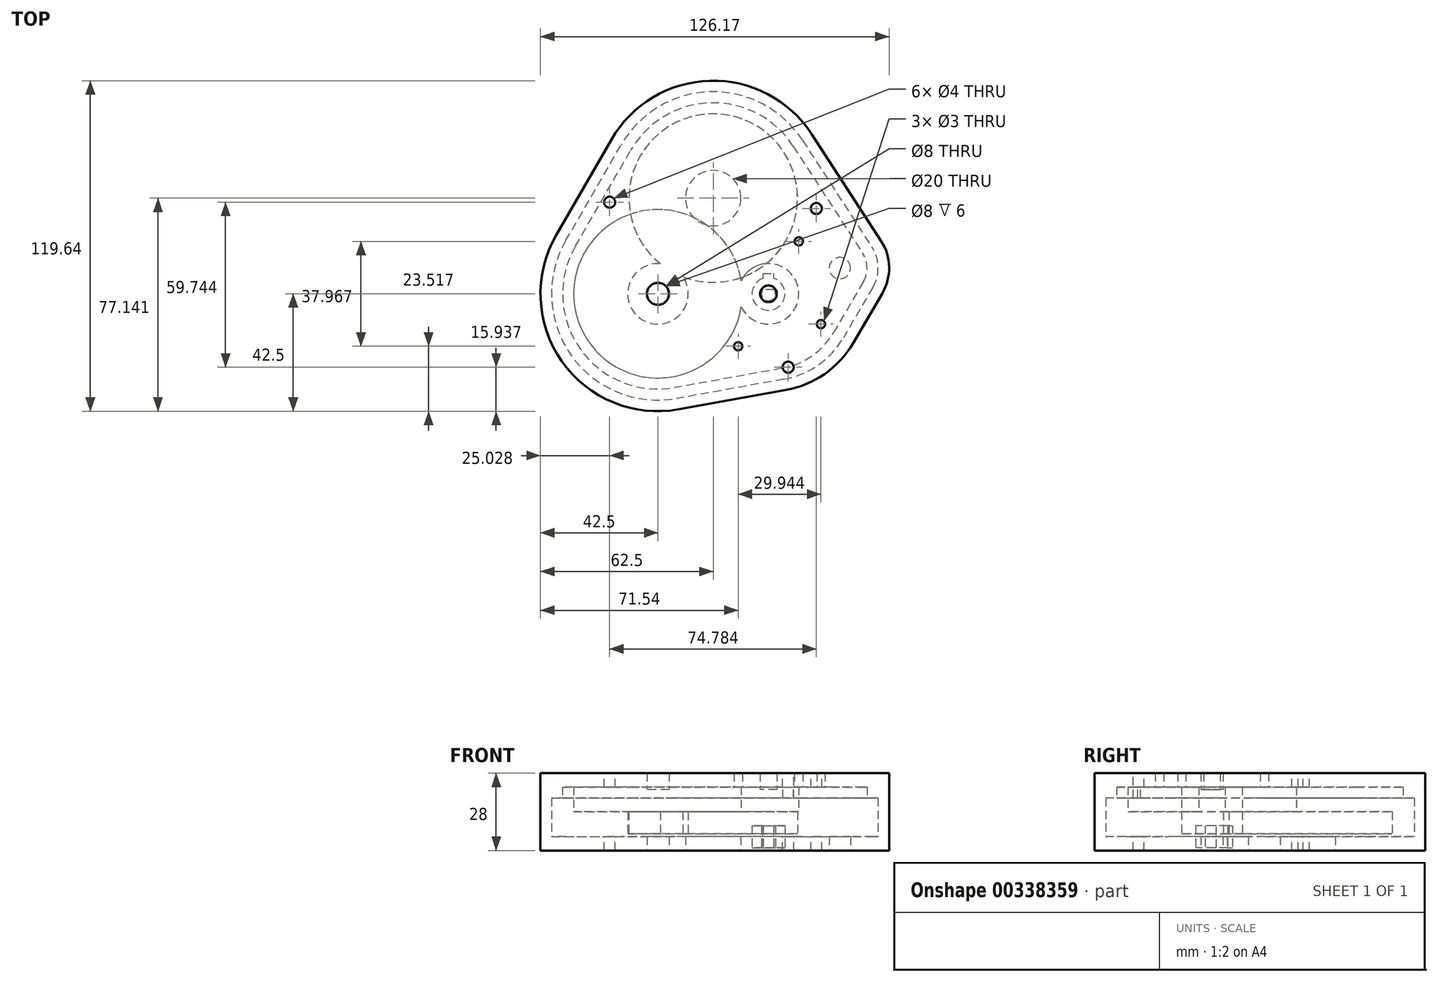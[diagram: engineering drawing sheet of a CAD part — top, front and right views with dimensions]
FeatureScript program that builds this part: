
annotation { "Feature Type Name" : "Feature", "Feature Type Description" : "" }
export const myFeature = defineFeature(function(context is Context, id is Id, definition is map)
    precondition{}
    {
        {
            var Q0;
            Q0=qCreatedBy(makeId("Top.planeOp"),FACE);
            var sketch = newSketch(context, id + "F0", { "sketchPlane" : qUnion([Q0])});
            skCircle(sketch, "E0", {"center": v(0, 0) * mm, "radius": 5.95 * mm});
            skLineSegment(sketch, "E1.bottom", {"start": v(-1.95, 5.62) * mm, "end": v(1.95, 5.62) * mm});
            skLineSegment(sketch, "E1.top", {"start": v(-1.95, 7.42) * mm, "end": v(1.95, 7.42) * mm});
            skLineSegment(sketch, "E1.left", {"start": v(-1.95, 5.62) * mm, "end": v(-1.95, 7.42) * mm});
            skLineSegment(sketch, "E1.right", {"start": v(1.95, 5.62) * mm, "end": v(1.95, 7.42) * mm});
            skLineSegment(sketch, "E2", {"start": v(0, 5.62) * mm, "end": v(0, 0) * mm, "construction": true});
            skCircle(sketch, "E3", {"center": v(0, 0) * mm, "radius": 2.5 * mm});
            skSolve(sketch);
        }
        {
            var Q0;
            {var subQ0=sQuery(id+"F0.wireOp",EDGE,"E1.bottom");Q0=makeQuery(id+"F0.imprint","IMPRINT",FACE,{"disambiguationData":[TD([[makeQuery(id+"F0.imprint","IMPRINT",EDGE,{"derivedFrom":subQ0}),-1.0]])]});}
            var Q1;
            {var subQ0=sQuery(id+"F0.wireOp",EDGE,"E1.bottom");Q1=makeQuery(id+"F0.imprint","IMPRINT",FACE,{"disambiguationData":[TD([[makeQuery(id+"F0.imprint","IMPRINT",EDGE,{"derivedFrom":subQ0}),1.0]])]});}
            var Q2;
            Q2=makeQuery(id+"F0.imprint","IMPRINT",FACE,{"disambiguationData":[TD([[makeQuery(id+"F0.imprint","IMPRINT",EDGE,{"derivedFrom":sQuery(id+"F0.wireOp",EDGE,"E1.top")}),-1.0]])]});
            extrude(context, id + "F1", {"entities" : qUnion([Q0, Q1, Q2]), "depth" : 8 * mm, "offsetDistance" : 25 * mm});
        }
        {
            var Q0;
            Q0=makeQuery(id+"F1.opExtrude","CAP_FACE",FACE,{"disambiguationData":[OSD([sQuery(id+"F0.wireOp",EDGE,"E0"),sQuery(id+"F0.wireOp",EDGE,"E1.top"),sQuery(id+"F0.wireOp",EDGE,"E1.left"),sQuery(id+"F0.wireOp",EDGE,"E1.right"),sQuery(id+"F0.wireOp",EDGE,"E3")])],"isStart":false});
            var sketch = newSketch(context, id + "F2", { "sketchPlane" : qUnion([Q0])});
            skLineSegment(sketch, "E4", {"start": v(-2, 1.5) * mm, "end": v(2, 1.5) * mm});
            skSolve(sketch);
        }
        {
            var Q0;
            {var subQ0=sQuery(id+"F2.wireOp",EDGE,"E4");Q0=makeQuery(id+"F2.imprint","IMPRINT",FACE,{"disambiguationData":[TD([[makeQuery(id+"F2.imprint","IMPRINT",EDGE,{"derivedFrom":subQ0}),1.0]])]});}
            var Q1;
            Q1=makeQuery(id+"F1.opExtrude","CAP_FACE",FACE,{"disambiguationData":[OSD([sQuery(id+"F0.wireOp",EDGE,"E0"),sQuery(id+"F0.wireOp",EDGE,"E1.top"),sQuery(id+"F0.wireOp",EDGE,"E1.left"),sQuery(id+"F0.wireOp",EDGE,"E1.right"),sQuery(id+"F0.wireOp",EDGE,"E3")])],"isStart":true});
            extrude(context, id + "F3", {"entities" : qUnion([Q0]), "operationType" : NewBodyOperationType.ADD, "endBound" : BoundingType.UP_TO_SURFACE, "oppositeDirection" : true, "depth" : 10 * mm, "endBoundEntityFace" : qUnion([Q1]), "offsetDistance" : 25 * mm});
        }
        {
            var Q0;
            Q0=qCreatedBy(makeId("Top.planeOp"),FACE);
            var sketch = newSketch(context, id + "F4", { "sketchPlane" : qUnion([Q0])});
            skCircle(sketch, "E5", {"center": v(-40, 0) * mm, "radius": 4 * mm});
            skLineSegment(sketch, "E6", {"start": v(-40, 0) * mm, "end": v(0, 0) * mm, "construction": true});
            skLineSegment(sketch, "E7", {"start": v(-40, 0) * mm, "end": v(-20, 34.64) * mm, "construction": true});
            skLineSegment(sketch, "E8", {"start": v(-20, 34.64) * mm, "end": v(0, 0) * mm, "construction": true});
            skCircle(sketch, "E9", {"center": v(-20, 34.64) * mm, "radius": 30.5 * mm, "construction": true});
            skCircle(sketch, "E10", {"center": v(-40, 0) * mm, "radius": 10.95 * mm, "construction": true});
            skCircle(sketch, "E11", {"center": v(-40, 0) * mm, "radius": 30.5 * mm, "construction": true});
            skCircle(sketch, "E12", {"center": v(0, 0) * mm, "radius": 10.95 * mm, "construction": true});
            skCircle(sketch, "E13", {"center": v(-20, 34.64) * mm, "radius": 10 * mm});
            skCircle(sketch, "E14", {"center": v(0, 0) * mm, "radius": 3 * mm});
            skCircle(sketch, "E15", {"center": v(-10.96, -18.98) * mm, "radius": 1.5 * mm});
            skCircle(sketch, "E16", {"center": v(10.96, 18.98) * mm, "radius": 1.5 * mm});
            skLineSegment(sketch, "E17", {"start": v(-10.96, -18.98) * mm, "end": v(0, 0) * mm, "construction": true});
            skLineSegment(sketch, "E18", {"start": v(0, 0) * mm, "end": v(10.96, 18.98) * mm, "construction": true});
            skLineSegment(sketch, "E19", {"start": v(-10.96, -18.98) * mm, "end": v(-14.6, -16.88) * mm, "construction": true});
            skLineSegment(sketch, "E20", {"start": v(10.96, 18.98) * mm, "end": v(7.32, 21.08) * mm, "construction": true});
            skCircle(sketch, "E21", {"center": v(18.98, -10.96) * mm, "radius": 1.5 * mm});
            skLineSegment(sketch, "E22", {"start": v(-10.96, -18.98) * mm, "end": v(18.98, -10.96) * mm, "construction": true});
            skLineSegment(sketch, "E23", {"start": v(18.98, -10.96) * mm, "end": v(10.96, 18.98) * mm, "construction": true});
            skCircle(sketch, "E24", {"center": v(25.82, 9.32) * mm, "radius": 3.85 * mm});
            skArc(sketch, "E25", {"start": v(-73.34, 19.25) * mm, "mid": v(-71.5, -22.14) * mm, "end": v(-33.19, -37.9) * mm});
            skArc(sketch, "E26", {"start": v(37.77, 2.32) * mm, "mid": v(39.66, 9.64) * mm, "end": v(37.44, 16.86) * mm});
            skArc(sketch, "E27", {"start": v(5.56, -30.92) * mm, "mid": v(17.99, -25.76) * mm, "end": v(27.11, -15.88) * mm});
            skLineSegment(sketch, "E28", {"start": v(-73.34, 19.25) * mm, "end": v(-53.34, 53.9) * mm});
            skLineSegment(sketch, "E29", {"start": v(12.3, 55.6) * mm, "end": v(37.44, 16.86) * mm});
            skLineSegment(sketch, "E30", {"start": v(37.77, 2.32) * mm, "end": v(27.11, -15.88) * mm});
            skLineSegment(sketch, "E31", {"start": v(5.56, -30.92) * mm, "end": v(-33.19, -37.9) * mm});
            skArc(sketch, "E32.trimOffspring", {"start": v(12.3, 55.6) * mm, "mid": v(-21, 73.13) * mm, "end": v(-53.34, 53.9) * mm});
            skLineSegment(sketch, "E33.0", {"start": v(-76.8, 21.25) * mm, "end": v(-56.8, 55.9) * mm});
            skArc(sketch, "E33.1", {"start": v(15.65, 57.78) * mm, "mid": v(-21.1, 77.13) * mm, "end": v(-56.8, 55.9) * mm});
            skArc(sketch, "E33.2", {"start": v(-76.8, 21.25) * mm, "mid": v(-74.77, -24.44) * mm, "end": v(-32.48, -41.83) * mm});
            skLineSegment(sketch, "E33.3", {"start": v(15.65, 57.78) * mm, "end": v(40.8, 19.04) * mm});
            skLineSegment(sketch, "E33.4", {"start": v(6.27, -34.86) * mm, "end": v(-32.48, -41.83) * mm});
            skArc(sketch, "E33.5", {"start": v(6.27, -34.86) * mm, "mid": v(20.28, -29.04) * mm, "end": v(30.57, -17.9) * mm});
            skLineSegment(sketch, "E33.6", {"start": v(41.22, 0.3) * mm, "end": v(30.57, -17.9) * mm});
            skArc(sketch, "E33.7", {"start": v(41.22, 0.3) * mm, "mid": v(43.66, 9.73) * mm, "end": v(40.8, 19.04) * mm});
            skSolve(sketch);
        }
        {
            var Q0;
            {var subQ0=sQuery(id+"F0.wireOp",EDGE,"E3");Q0=makeQuery(id+"F3.boolean.opBoolean","MERGE",FACE,{"derivedFrom":[makeQuery(id+"F1.opExtrude","CAP_FACE",FACE,{"disambiguationData":[OSD([sQuery(id+"F0.wireOp",EDGE,"E0"),sQuery(id+"F0.wireOp",EDGE,"E1.top"),sQuery(id+"F0.wireOp",EDGE,"E1.left"),sQuery(id+"F0.wireOp",EDGE,"E1.right"),subQ0])],"isStart":true}),makeQuery(id+"F3.opExtrude","CAP_FACE",FACE,{"disambiguationData":[OSD([subQ0,sQuery(id+"F2.wireOp",EDGE,"E4")])],"isStart":false})]});}
            extrude(context, id + "F5", {"entities" : qUnion([Q0]), "operationType" : NewBodyOperationType.REMOVE, "oppositeDirection" : true, "depth" : 1 * mm, "offsetDistance" : 25 * mm});
        }
        {
            var Q0;
            {var subQ0=sQuery(id+"F0.wireOp",EDGE,"E3");Q0=makeQuery(id+"F3.boolean.opBoolean","MERGE",FACE,{"derivedFrom":[makeQuery(id+"F1.opExtrude","CAP_FACE",FACE,{"disambiguationData":[OSD([sQuery(id+"F0.wireOp",EDGE,"E0"),sQuery(id+"F0.wireOp",EDGE,"E1.top"),sQuery(id+"F0.wireOp",EDGE,"E1.left"),sQuery(id+"F0.wireOp",EDGE,"E1.right"),subQ0])],"isStart":false}),makeQuery(id+"F3.opExtrude","CAP_FACE",FACE,{"disambiguationData":[OSD([subQ0,sQuery(id+"F2.wireOp",EDGE,"E4")])],"isStart":true})]});}
            extrude(context, id + "F6", {"entities" : qUnion([Q0]), "operationType" : NewBodyOperationType.ADD, "depth" : 1 * mm, "offsetDistance" : 25 * mm});
        }
        {
            var Q0;
            Q0=makeQuery(id+"F4.imprint","IMPRINT",FACE,{"disambiguationData":[TD([[makeQuery(id+"F4.imprint","IMPRINT",EDGE,{"derivedFrom":sQuery(id+"F4.wireOp",EDGE,"E5")}),-1.0]])]});
            var Q1;
            Q1=makeQuery(id+"F4.imprint","IMPRINT",FACE,{"disambiguationData":[TD([[makeQuery(id+"F4.imprint","IMPRINT",EDGE,{"derivedFrom":sQuery(id+"F4.wireOp",EDGE,"E15")}),1.0]])]});
            var Q2;
            Q2=makeQuery(id+"F4.imprint","IMPRINT",FACE,{"disambiguationData":[TD([[makeQuery(id+"F4.imprint","IMPRINT",EDGE,{"derivedFrom":sQuery(id+"F4.wireOp",EDGE,"E14")}),1.0]])]});
            var Q3;
            Q3=makeQuery(id+"F4.imprint","IMPRINT",FACE,{"disambiguationData":[TD([[makeQuery(id+"F4.imprint","IMPRINT",EDGE,{"derivedFrom":sQuery(id+"F4.wireOp",EDGE,"E21")}),1.0]])]});
            var Q4;
            Q4=makeQuery(id+"F4.imprint","IMPRINT",FACE,{"disambiguationData":[TD([[makeQuery(id+"F4.imprint","IMPRINT",EDGE,{"derivedFrom":sQuery(id+"F4.wireOp",EDGE,"E16")}),1.0]])]});
            extrude(context, id + "F7", {"entities" : qUnion([Q0, Q1, Q2, Q3, Q4]), "depth" : 5 * mm, "offsetDistance" : 25 * mm});
        }
        {
            var Q0;
            Q0=makeQuery(id+"F4.imprint","IMPRINT",FACE,{"disambiguationData":[TD([[makeQuery(id+"F4.imprint","IMPRINT",EDGE,{"derivedFrom":sQuery(id+"F4.wireOp",EDGE,"E25")}),-1.0]])]});
            extrude(context, id + "F8", {"entities" : qUnion([Q0]), "operationType" : NewBodyOperationType.ADD, "depth" : (18 + 5) * mm, "offsetDistance" : 25 * mm});
        }
        {
            var Q0;
            Q0=makeQuery(id+"F7.opExtrude","CAP_FACE",FACE,{"disambiguationData":[OSD([sQuery(id+"F4.wireOp",EDGE,"E5"),sQuery(id+"F4.wireOp",EDGE,"E13"),sQuery(id+"F4.wireOp",EDGE,"E24"),sQuery(id+"F4.wireOp",EDGE,"E25"),sQuery(id+"F4.wireOp",EDGE,"E26"),sQuery(id+"F4.wireOp",EDGE,"E27"),sQuery(id+"F4.wireOp",EDGE,"E28"),sQuery(id+"F4.wireOp",EDGE,"E29"),sQuery(id+"F4.wireOp",EDGE,"E30"),sQuery(id+"F4.wireOp",EDGE,"E31"),sQuery(id+"F4.wireOp",EDGE,"E32.trimOffspring")])],"isStart":false});
            cPlane(context, id + "F9", {"entities" : qUnion([Q0]), "cplaneType" : CPlaneType.OFFSET, "offset" : 1 * mm, "width" : 150 * mm, "height" : 150 * mm});
        }
        {
            var Q0;
            Q0=qCreatedBy(id+"F9.planeOp",FACE);
            var sketch = newSketch(context, id + "F10", { "sketchPlane" : qUnion([Q0])});
            skCircle(sketch, "E34.0", {"center": v(-20, 34.64) * mm, "radius": 30.5 * mm});
            skCircle(sketch, "E35.0", {"center": v(-40, 0) * mm, "radius": 10.95 * mm});
            skSolve(sketch);
        }
        {
            var Q0;
            {var subQ0=sQuery(id+"F10.wireOp",EDGE,"E35.0");var subQ1=sQuery(id+"F10.wireOp",EDGE,"E34.0");var subQ2=makeQuery(id+"F10.imprint","INTERSECT",VERTEX,{"disambiguationData":[OD(0.0)],"derivedFrom":[subQ1,subQ0]});Q0=makeQuery(id+"F10.imprint","IMPRINT",FACE,{"disambiguationData":[TD([[makeQuery(id+"F10.imprint","IMPRINT",EDGE,{"disambiguationData":[TD([[subQ2,1.0]])],"derivedFrom":subQ1}),1.0]])]});}
            var Q1;
            {var subQ0=sQuery(id+"F10.wireOp",EDGE,"E35.0");var subQ1=sQuery(id+"F10.wireOp",EDGE,"E34.0");var subQ2=makeQuery(id+"F10.imprint","INTERSECT",VERTEX,{"disambiguationData":[OD(0.0)],"derivedFrom":[subQ1,subQ0]});Q1=makeQuery(id+"F10.imprint","IMPRINT",FACE,{"disambiguationData":[TD([[makeQuery(id+"F10.imprint","IMPRINT",EDGE,{"disambiguationData":[TD([[subQ2,-1.0]])],"derivedFrom":subQ1}),1.0]])]});}
            var Q2;
            {var subQ0=sQuery(id+"F10.wireOp",EDGE,"E35.0");var subQ1=sQuery(id+"F10.wireOp",EDGE,"E34.0");var subQ2=makeQuery(id+"F10.imprint","INTERSECT",VERTEX,{"disambiguationData":[OD(0.0)],"derivedFrom":[subQ1,subQ0]});Q2=makeQuery(id+"F10.imprint","IMPRINT",FACE,{"disambiguationData":[TD([[makeQuery(id+"F10.imprint","IMPRINT",EDGE,{"disambiguationData":[TD([[subQ2,-1.0]])],"derivedFrom":subQ1}),-1.0]])]});}
            extrude(context, id + "F11", {"entities" : qUnion([Q0, Q1, Q2]), "depth" : 8 * mm, "offsetDistance" : 25 * mm});
        }
        {
            var Q0;
            Q0=makeQuery(id+"F11.opExtrude","CAP_FACE",FACE,{"disambiguationData":[OSD([sQuery(id+"F10.wireOp",EDGE,"E34.0"),sQuery(id+"F10.wireOp",EDGE,"E35.0")])],"isStart":false});
            var sketch = newSketch(context, id + "F12", { "sketchPlane" : qUnion([Q0])});
            skCircle(sketch, "E36.0", {"center": v(-40, 0) * mm, "radius": 30.5 * mm});
            skCircle(sketch, "E37.0", {"center": v(0, 0) * mm, "radius": 10.95 * mm});
            skSolve(sketch);
        }
        {
            var Q0;
            {var subQ4=makeQuery(id+"F11.opExtrude","CAP_EDGE",EDGE,{"disambiguationData":[OSD([sQuery(id+"F10.wireOp",EDGE,"E35.0")])],"isStart":false});Q0=makeQuery(id+"F12.imprint","IMPRINT",FACE,{"disambiguationData":[TD([[makeQuery(id+"F12.imprint","IMPRINT",EDGE,{"derivedFrom":subQ4}),1.0]])]});}
            var Q1;
            {var subQ0=makeQuery(id+"F11.opExtrude","CAP_EDGE",EDGE,{"disambiguationData":[OSD([sQuery(id+"F10.wireOp",EDGE,"E35.0")])],"isStart":false});Q1=makeQuery(id+"F12.imprint","IMPRINT",FACE,{"disambiguationData":[TD([[makeQuery(id+"F12.imprint","IMPRINT",EDGE,{"derivedFrom":subQ0}),-1.0]])]});}
            var Q2;
            {var subQ0=sQuery(id+"F12.wireOp",EDGE,"E37.0");var subQ1=sQuery(id+"F12.wireOp",EDGE,"E36.0");var subQ2=makeQuery(id+"F12.imprint","INTERSECT",VERTEX,{"disambiguationData":[OD(0.0)],"derivedFrom":[subQ1,subQ0]});Q2=makeQuery(id+"F12.imprint","IMPRINT",FACE,{"disambiguationData":[TD([[makeQuery(id+"F12.imprint","IMPRINT",EDGE,{"disambiguationData":[TD([[subQ2,-1.0]])],"derivedFrom":subQ1}),1.0]])]});}
            var Q3;
            {var subQ0=sQuery(id+"F12.wireOp",EDGE,"E37.0");var subQ1=sQuery(id+"F12.wireOp",EDGE,"E36.0");var subQ2=makeQuery(id+"F12.imprint","INTERSECT",VERTEX,{"disambiguationData":[OD(0.0)],"derivedFrom":[subQ1,subQ0]});Q3=makeQuery(id+"F12.imprint","IMPRINT",FACE,{"disambiguationData":[TD([[makeQuery(id+"F12.imprint","IMPRINT",EDGE,{"disambiguationData":[TD([[subQ2,-1.0]])],"derivedFrom":subQ1}),-1.0]])]});}
            var Q4;
            {var subQ0=sQuery(id+"F12.wireOp",EDGE,"E37.0");var subQ1=makeQuery(id+"F11.opExtrude","CAP_EDGE",EDGE,{"disambiguationData":[OSD([sQuery(id+"F10.wireOp",EDGE,"E34.0")])],"isStart":false});var subQ2=makeQuery(id+"F12.imprint","INTERSECT",VERTEX,{"disambiguationData":[OD(0.0)],"derivedFrom":[subQ1,subQ0]});Q4=makeQuery(id+"F12.imprint","IMPRINT",FACE,{"disambiguationData":[TD([[makeQuery(id+"F12.imprint","IMPRINT",EDGE,{"disambiguationData":[TD([[subQ2,-1.0]])],"derivedFrom":subQ0}),1.0]])]});}
            extrude(context, id + "F13", {"entities" : qUnion([Q0, Q1, Q2, Q3, Q4]), "operationType" : NewBodyOperationType.ADD, "depth" : 8 * mm, "offsetDistance" : 25 * mm});
        }
        {
            var Q0;
            Q0=makeQuery(id+"F8.opExtrude","CAP_FACE",FACE,{"disambiguationData":[OSD([sQuery(id+"F4.wireOp",EDGE,"E25"),sQuery(id+"F4.wireOp",EDGE,"E26"),sQuery(id+"F4.wireOp",EDGE,"E27"),sQuery(id+"F4.wireOp",EDGE,"E28"),sQuery(id+"F4.wireOp",EDGE,"E29"),sQuery(id+"F4.wireOp",EDGE,"E30"),sQuery(id+"F4.wireOp",EDGE,"E31"),sQuery(id+"F4.wireOp",EDGE,"E32.trimOffspring"),sQuery(id+"F4.wireOp",EDGE,"E33.0"),sQuery(id+"F4.wireOp",EDGE,"E33.1"),sQuery(id+"F4.wireOp",EDGE,"E33.2"),sQuery(id+"F4.wireOp",EDGE,"E33.3"),sQuery(id+"F4.wireOp",EDGE,"E33.4"),sQuery(id+"F4.wireOp",EDGE,"E33.5"),sQuery(id+"F4.wireOp",EDGE,"E33.6"),sQuery(id+"F4.wireOp",EDGE,"E33.7")])],"isStart":false});
            var sketch = newSketch(context, id + "F14", { "sketchPlane" : qUnion([Q0])});
            skCircle(sketch, "E38.0", {"center": v(0, 0) * mm, "radius": 3 * mm});
            skCircle(sketch, "E39.0", {"center": v(10.96, 18.98) * mm, "radius": 1.5 * mm});
            skCircle(sketch, "E40.0", {"center": v(18.98, -10.96) * mm, "radius": 1.5 * mm});
            skCircle(sketch, "E41.0", {"center": v(-10.96, -18.98) * mm, "radius": 1.5 * mm});
            skCircle(sketch, "E42.0", {"center": v(-40, 0) * mm, "radius": 4 * mm});
            skLineSegment(sketch, "E43.0.0", {"start": v(30.57, -17.9) * mm, "end": v(41.22, 0.3) * mm});
            skArc(sketch, "E43.0.1", {"start": v(41.22, 0.3) * mm, "mid": v(43.66, 9.73) * mm, "end": v(40.8, 19.04) * mm});
            skLineSegment(sketch, "E43.0.2", {"start": v(40.8, 19.04) * mm, "end": v(15.65, 57.78) * mm});
            skArc(sketch, "E43.0.3", {"start": v(15.65, 57.78) * mm, "mid": v(-21.1, 77.13) * mm, "end": v(-56.8, 55.9) * mm});
            skLineSegment(sketch, "E43.0.4", {"start": v(-56.8, 55.9) * mm, "end": v(-76.8, 21.25) * mm});
            skArc(sketch, "E43.0.5", {"start": v(-76.8, 21.25) * mm, "mid": v(-74.77, -24.44) * mm, "end": v(-32.48, -41.83) * mm});
            skLineSegment(sketch, "E43.0.6", {"start": v(-32.48, -41.83) * mm, "end": v(6.27, -34.86) * mm});
            skArc(sketch, "E43.0.7", {"start": v(6.27, -34.86) * mm, "mid": v(20.28, -29.04) * mm, "end": v(30.57, -17.9) * mm});
            skArc(sketch, "E44.0", {"start": v(5.56, -30.92) * mm, "mid": v(17.99, -25.76) * mm, "end": v(27.11, -15.88) * mm});
            skLineSegment(sketch, "E45.0", {"start": v(5.56, -30.92) * mm, "end": v(-33.19, -37.9) * mm});
            skLineSegment(sketch, "E46.0", {"start": v(37.77, 2.32) * mm, "end": v(27.11, -15.88) * mm});
            skArc(sketch, "E47.0", {"start": v(37.77, 2.32) * mm, "mid": v(39.66, 9.64) * mm, "end": v(37.44, 16.86) * mm});
            skLineSegment(sketch, "E48.0", {"start": v(12.3, 55.6) * mm, "end": v(37.44, 16.86) * mm});
            skArc(sketch, "E49.0", {"start": v(12.3, 55.6) * mm, "mid": v(-21, 73.13) * mm, "end": v(-53.34, 53.9) * mm});
            skLineSegment(sketch, "E50.0", {"start": v(-73.34, 19.25) * mm, "end": v(-53.34, 53.9) * mm});
            skArc(sketch, "E51.0", {"start": v(-73.34, 19.25) * mm, "mid": v(-71.5, -22.14) * mm, "end": v(-33.19, -37.9) * mm});
            skSolve(sketch);
        }
        {
            var Q0;
            Q0=makeQuery(id+"F14.imprint","IMPRINT",FACE,{"disambiguationData":[TD([[makeQuery(id+"F14.imprint","IMPRINT",EDGE,{"derivedFrom":sQuery(id+"F14.wireOp",EDGE,"E38.0")}),-1.0]])]});
            var Q1;
            Q1=makeQuery(id+"F14.imprint","IMPRINT",FACE,{"disambiguationData":[TD([[makeQuery(id+"F14.imprint","IMPRINT",EDGE,{"derivedFrom":sQuery(id+"F14.wireOp",EDGE,"E43.0.0")}),-1.0]])]});
            extrude(context, id + "F15", {"entities" : qUnion([Q0, Q1]), "depth" : 5 * mm, "offsetDistance" : 25 * mm});
        }
        {
            var Q0;
            Q0=makeQuery(id+"F14.imprint","IMPRINT",FACE,{"disambiguationData":[TD([[makeQuery(id+"F14.imprint","IMPRINT",EDGE,{"derivedFrom":sQuery(id+"F14.wireOp",EDGE,"E38.0")}),-1.0]])]});
            extrude(context, id + "F16", {"entities" : qUnion([Q0]), "operationType" : NewBodyOperationType.ADD, "oppositeDirection" : true, "depth" : 4 * mm, "offsetDistance" : 25 * mm});
        }
        {
            var Q0;
            Q0=makeQuery(id+"F16.opExtrude","CAP_FACE",FACE,{"disambiguationData":[OSD([sQuery(id+"F14.wireOp",EDGE,"E38.0"),sQuery(id+"F14.wireOp",EDGE,"E39.0"),sQuery(id+"F14.wireOp",EDGE,"E40.0"),sQuery(id+"F14.wireOp",EDGE,"E41.0"),sQuery(id+"F14.wireOp",EDGE,"E42.0"),sQuery(id+"F14.wireOp",EDGE,"E44.0"),sQuery(id+"F14.wireOp",EDGE,"E45.0"),sQuery(id+"F14.wireOp",EDGE,"E46.0"),sQuery(id+"F14.wireOp",EDGE,"E47.0"),sQuery(id+"F14.wireOp",EDGE,"E48.0"),sQuery(id+"F14.wireOp",EDGE,"E49.0"),sQuery(id+"F14.wireOp",EDGE,"E50.0"),sQuery(id+"F14.wireOp",EDGE,"E51.0")])],"isStart":false});
            var sketch = newSketch(context, id + "F17", { "sketchPlane" : qUnion([Q0])});
            skArc(sketch, "E52.0", {"start": v(34.08, -14.68) * mm, "mid": v(35.67, -9.54) * mm, "end": v(34.32, -4.34) * mm});
            skLineSegment(sketch, "E52.1", {"start": v(8.94, -53.42) * mm, "end": v(34.08, -14.68) * mm});
            skLineSegment(sketch, "E52.2", {"start": v(34.32, -4.34) * mm, "end": v(23.66, 13.86) * mm});
            skArc(sketch, "E52.3", {"start": v(-49.88, -51.9) * mm, "mid": v(-20.9, -69.13) * mm, "end": v(8.94, -53.42) * mm});
            skArc(sketch, "E52.4", {"start": v(23.66, 13.86) * mm, "mid": v(15.7, 22.48) * mm, "end": v(4.85, 26.99) * mm});
            skLineSegment(sketch, "E52.5", {"start": v(4.85, 26.99) * mm, "end": v(-33.9, 33.96) * mm});
            skArc(sketch, "E52.6", {"start": v(-33.9, 33.96) * mm, "mid": v(-68.23, 19.84) * mm, "end": v(-69.88, -17.25) * mm});
            skLineSegment(sketch, "E52.7", {"start": v(-69.88, -17.25) * mm, "end": v(-49.88, -51.9) * mm});
            skSolve(sketch);
        }
        {
            var Q0;
            Q0=makeQuery(id+"F17.imprint","IMPRINT",FACE,{"disambiguationData":[TD([[makeQuery(id+"F17.imprint","IMPRINT",EDGE,{"derivedFrom":sQuery(id+"F17.wireOp",EDGE,"E52.0")}),1.0]])]});
            extrude(context, id + "F18", {"entities" : qUnion([Q0]), "operationType" : NewBodyOperationType.REMOVE, "oppositeDirection" : true, "depth" : 4 * mm, "offsetDistance" : 25 * mm});
        }
        {
            var Q0;
            Q0=makeQuery(id+"F15.opExtrude","CAP_FACE",FACE,{"disambiguationData":[OSD([sQuery(id+"F14.wireOp",EDGE,"E38.0"),sQuery(id+"F14.wireOp",EDGE,"E39.0"),sQuery(id+"F14.wireOp",EDGE,"E40.0"),sQuery(id+"F14.wireOp",EDGE,"E41.0"),sQuery(id+"F14.wireOp",EDGE,"E42.0"),sQuery(id+"F14.wireOp",EDGE,"E43.0.0"),sQuery(id+"F14.wireOp",EDGE,"E43.0.1"),sQuery(id+"F14.wireOp",EDGE,"E43.0.2"),sQuery(id+"F14.wireOp",EDGE,"E43.0.3"),sQuery(id+"F14.wireOp",EDGE,"E43.0.4"),sQuery(id+"F14.wireOp",EDGE,"E43.0.5"),sQuery(id+"F14.wireOp",EDGE,"E43.0.6"),sQuery(id+"F14.wireOp",EDGE,"E43.0.7")])],"isStart":false});
            var sketch = newSketch(context, id + "F19", { "sketchPlane" : qUnion([Q0])});
            skCircle(sketch, "E53", {"center": v(-57.47, 33.18) * mm, "radius": 2 * mm});
            skCircle(sketch, "E54", {"center": v(7.12, -26.56) * mm, "radius": 2 * mm});
            skLineSegment(sketch, "E55", {"start": v(-10.96, -18.98) * mm, "end": v(18.98, -10.96) * mm, "construction": true});
            skLineSegment(sketch, "E56", {"start": v(4.01, -14.97) * mm, "end": v(7.12, -26.56) * mm, "construction": true});
            skCircle(sketch, "E57", {"center": v(17.31, 30.9) * mm, "radius": 2 * mm});
            skSolve(sketch);
        }
        {
            var Q0;
            Q0=makeQuery(id+"F19.imprint","IMPRINT",FACE,{"disambiguationData":[TD([[makeQuery(id+"F19.imprint","IMPRINT",EDGE,{"derivedFrom":sQuery(id+"F19.wireOp",EDGE,"E53")}),1.0]])]});
            var Q1;
            Q1=makeQuery(id+"F19.imprint","IMPRINT",FACE,{"disambiguationData":[TD([[makeQuery(id+"F19.imprint","IMPRINT",EDGE,{"derivedFrom":sQuery(id+"F19.wireOp",EDGE,"E57")}),1.0]])]});
            var Q2;
            Q2=makeQuery(id+"F19.imprint","IMPRINT",FACE,{"disambiguationData":[TD([[makeQuery(id+"F19.imprint","IMPRINT",EDGE,{"derivedFrom":sQuery(id+"F19.wireOp",EDGE,"E54")}),1.0]])]});
            extrude(context, id + "F20", {"entities" : qUnion([Q0, Q1, Q2]), "operationType" : NewBodyOperationType.REMOVE, "oppositeDirection" : true, "depth" : 40 * mm, "offsetDistance" : 25 * mm});
        }
    });
